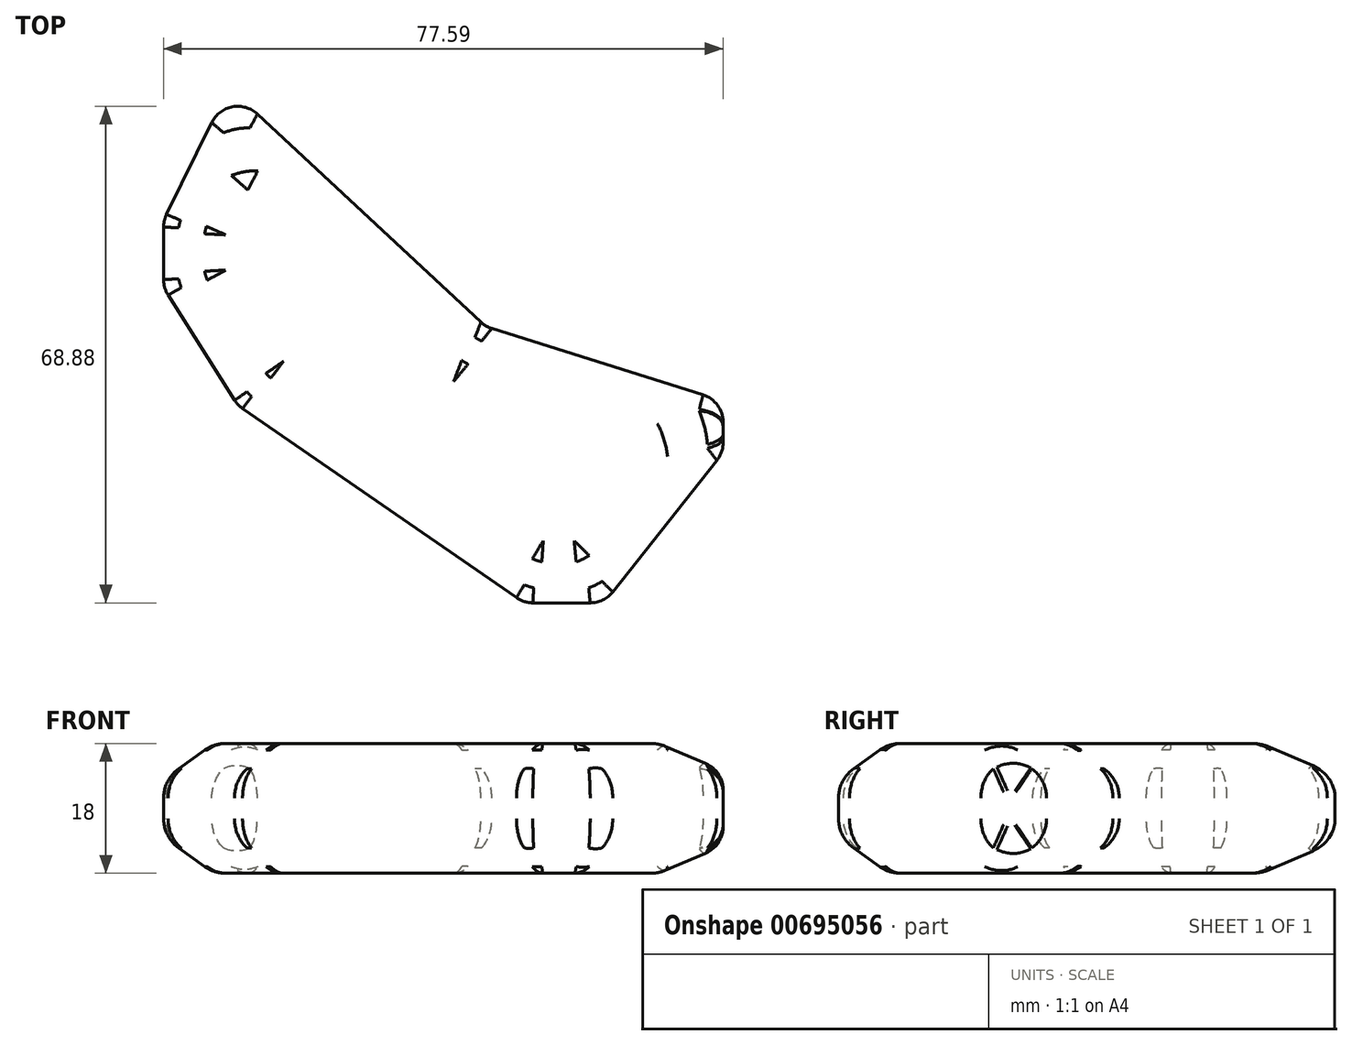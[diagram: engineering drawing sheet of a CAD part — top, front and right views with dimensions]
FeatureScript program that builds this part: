
annotation { "Feature Type Name" : "Feature", "Feature Type Description" : "" }
export const myFeature = defineFeature(function(context is Context, id is Id, definition is map)
    precondition{}
    {
        {
            var Q0;
            Q0=qCreatedBy(makeId("Top.planeOp"),FACE);
            var sketch = newSketch(context, id + "F0", { "sketchPlane" : qUnion([Q0])});
            skCircle(sketch, "E0", {"center": v(11.86, 12.18) * mm, "radius": 17 * mm, "construction": true});
            skLineSegment(sketch, "E1", {"start": v(0, 0) * mm, "end": v(35.6, -33.14) * mm});
            skLineSegment(sketch, "E2", {"start": v(35.6, -33.14) * mm, "end": v(68.53, -43.5) * mm});
            skLineSegment(sketch, "E3", {"start": v(68.53, -43.5) * mm, "end": v(68.53, -50.63) * mm});
            skLineSegment(sketch, "E4", {"start": v(68.53, -50.63) * mm, "end": v(52.03, -71.47) * mm});
            skLineSegment(sketch, "E5", {"start": v(52.03, -71.47) * mm, "end": v(40.9, -71.47) * mm});
            skLineSegment(sketch, "E6", {"start": v(40.9, -71.47) * mm, "end": v(1.22, -44.06) * mm});
            skLineSegment(sketch, "E7", {"start": v(1.22, -44.06) * mm, "end": v(-9.06, -27.79) * mm});
            skLineSegment(sketch, "E8", {"start": v(-9.06, -27.79) * mm, "end": v(-9.06, -18.41) * mm});
            skLineSegment(sketch, "E9", {"start": v(-9.06, -18.41) * mm, "end": v(0, 0) * mm});
            skSolve(sketch);
        }
        {
            var Q0;
            Q0=makeQuery(id+"F0.imprint","IMPRINT",FACE,{"disambiguationData":[TD([[makeQuery(id+"F0.imprint","IMPRINT",EDGE,{"derivedFrom":sQuery(id+"F0.wireOp",EDGE,"E1")}),-1.0]])]});
            extrude(context, id + "F1", {"entities" : qUnion([Q0]), "depth" : 9 * mm, "offsetDistance" : 25 * mm, "hasSecondDirection" : true, "secondDirectionOppositeDirection" : true, "secondDirectionDepth" : 9 * mm});
        }
        {
            var Q0;
            Q0=makeQuery(id+"F1.opExtrude","CAP_FACE",FACE,{"disambiguationData":[OSD([sQuery(id+"F0.wireOp",EDGE,"E1"),sQuery(id+"F0.wireOp",EDGE,"E2"),sQuery(id+"F0.wireOp",EDGE,"E3"),sQuery(id+"F0.wireOp",EDGE,"E4"),sQuery(id+"F0.wireOp",EDGE,"E5"),sQuery(id+"F0.wireOp",EDGE,"E6"),sQuery(id+"F0.wireOp",EDGE,"E7"),sQuery(id+"F0.wireOp",EDGE,"E8"),sQuery(id+"F0.wireOp",EDGE,"E9")])],"isStart":false});
            chamfer(context, id + "F2", {"entities" : qUnion([Q0]), "chamferType" : ChamferType.TWO_OFFSETS, "width1" : 5 * mm, "oppositeDirection" : false, "width2" : 7 * mm, "tangentPropagation" : true});
        }
        {
            var Q0;
            Q0=makeQuery(id+"F1.opExtrude","CAP_FACE",FACE,{"disambiguationData":[OSD([sQuery(id+"F0.wireOp",EDGE,"E1"),sQuery(id+"F0.wireOp",EDGE,"E2"),sQuery(id+"F0.wireOp",EDGE,"E3"),sQuery(id+"F0.wireOp",EDGE,"E4"),sQuery(id+"F0.wireOp",EDGE,"E5"),sQuery(id+"F0.wireOp",EDGE,"E6"),sQuery(id+"F0.wireOp",EDGE,"E7"),sQuery(id+"F0.wireOp",EDGE,"E8"),sQuery(id+"F0.wireOp",EDGE,"E9")])],"isStart":true});
            chamfer(context, id + "F3", {"entities" : qUnion([Q0]), "chamferType" : ChamferType.TWO_OFFSETS, "width1" : 7 * mm, "oppositeDirection" : false, "width2" : 5 * mm, "tangentPropagation" : true});
        }
        {
            var Q0;
            Q0=makeQuery(id+"F1.opExtrude","CAP_FACE",FACE,{"disambiguationData":[OSD([sQuery(id+"F0.wireOp",EDGE,"E1"),sQuery(id+"F0.wireOp",EDGE,"E2"),sQuery(id+"F0.wireOp",EDGE,"E3"),sQuery(id+"F0.wireOp",EDGE,"E4"),sQuery(id+"F0.wireOp",EDGE,"E5"),sQuery(id+"F0.wireOp",EDGE,"E6"),sQuery(id+"F0.wireOp",EDGE,"E7"),sQuery(id+"F0.wireOp",EDGE,"E8"),sQuery(id+"F0.wireOp",EDGE,"E9")])],"isStart":true});
            var Q1;
            Q1=makeQuery(id+"F1.opExtrude","CAP_FACE",FACE,{"disambiguationData":[OSD([sQuery(id+"F0.wireOp",EDGE,"E1"),sQuery(id+"F0.wireOp",EDGE,"E2"),sQuery(id+"F0.wireOp",EDGE,"E3"),sQuery(id+"F0.wireOp",EDGE,"E4"),sQuery(id+"F0.wireOp",EDGE,"E5"),sQuery(id+"F0.wireOp",EDGE,"E6"),sQuery(id+"F0.wireOp",EDGE,"E7"),sQuery(id+"F0.wireOp",EDGE,"E8"),sQuery(id+"F0.wireOp",EDGE,"E9")])],"isStart":false});
            var Q2;
            {var subQ0=sQuery(id+"F0.wireOp",EDGE,"E2");Q2=makeQuery(id+"F3.opChamfer","BLEND_EDGE",EDGE,{"blendedFrom":[makeQuery(id+"F1.opExtrude","CAP_EDGE",EDGE,{"disambiguationData":[OSD([subQ0])],"isStart":true}),makeQuery(id+"F1.opExtrude","SWEPT_FACE",FACE,{"disambiguationData":[OSD([subQ0])]})],"blendedInto":[makeQuery(id+"F1.opExtrude","SWEPT_FACE",FACE,{"disambiguationData":[OSD([subQ0])]})]});}
            var Q3;
            {var subQ0=sQuery(id+"F0.wireOp",EDGE,"E2");Q3=makeQuery(id+"F2.opChamfer","BLEND_EDGE",EDGE,{"blendedFrom":[makeQuery(id+"F1.opExtrude","CAP_EDGE",EDGE,{"disambiguationData":[OSD([subQ0])],"isStart":false}),makeQuery(id+"F1.opExtrude","SWEPT_FACE",FACE,{"disambiguationData":[OSD([subQ0])]})],"blendedInto":[makeQuery(id+"F1.opExtrude","SWEPT_FACE",FACE,{"disambiguationData":[OSD([subQ0])]})]});}
            var Q4;
            {var subQ0=sQuery(id+"F0.wireOp",EDGE,"E1");Q4=makeQuery(id+"F2.opChamfer","BLEND_EDGE",EDGE,{"blendedFrom":[makeQuery(id+"F1.opExtrude","CAP_EDGE",EDGE,{"disambiguationData":[OSD([subQ0])],"isStart":false}),makeQuery(id+"F1.opExtrude","SWEPT_FACE",FACE,{"disambiguationData":[OSD([subQ0])]})],"blendedInto":[makeQuery(id+"F1.opExtrude","SWEPT_FACE",FACE,{"disambiguationData":[OSD([subQ0])]})]});}
            var Q5;
            {var subQ0=sQuery(id+"F0.wireOp",EDGE,"E1");Q5=makeQuery(id+"F3.opChamfer","BLEND_EDGE",EDGE,{"blendedFrom":[makeQuery(id+"F1.opExtrude","CAP_EDGE",EDGE,{"disambiguationData":[OSD([subQ0])],"isStart":true}),makeQuery(id+"F1.opExtrude","SWEPT_FACE",FACE,{"disambiguationData":[OSD([subQ0])]})],"blendedInto":[makeQuery(id+"F1.opExtrude","SWEPT_FACE",FACE,{"disambiguationData":[OSD([subQ0])]})]});}
            var Q6;
            {var subQ0=sQuery(id+"F0.wireOp",EDGE,"E9");Q6=makeQuery(id+"F3.opChamfer","BLEND_EDGE",EDGE,{"blendedFrom":[makeQuery(id+"F1.opExtrude","CAP_EDGE",EDGE,{"disambiguationData":[OSD([subQ0])],"isStart":true}),makeQuery(id+"F1.opExtrude","SWEPT_FACE",FACE,{"disambiguationData":[OSD([subQ0])]})],"blendedInto":[makeQuery(id+"F1.opExtrude","SWEPT_FACE",FACE,{"disambiguationData":[OSD([subQ0])]})]});}
            var Q7;
            {var subQ0=sQuery(id+"F0.wireOp",EDGE,"E9");Q7=makeQuery(id+"F2.opChamfer","BLEND_EDGE",EDGE,{"blendedFrom":[makeQuery(id+"F1.opExtrude","CAP_EDGE",EDGE,{"disambiguationData":[OSD([subQ0])],"isStart":false}),makeQuery(id+"F1.opExtrude","SWEPT_FACE",FACE,{"disambiguationData":[OSD([subQ0])]})],"blendedInto":[makeQuery(id+"F1.opExtrude","SWEPT_FACE",FACE,{"disambiguationData":[OSD([subQ0])]})]});}
            var Q8;
            {var subQ0=sQuery(id+"F0.wireOp",EDGE,"E4");Q8=makeQuery(id+"F3.opChamfer","BLEND_EDGE",EDGE,{"blendedFrom":[makeQuery(id+"F1.opExtrude","CAP_EDGE",EDGE,{"disambiguationData":[OSD([subQ0])],"isStart":true}),makeQuery(id+"F1.opExtrude","SWEPT_FACE",FACE,{"disambiguationData":[OSD([subQ0])]})],"blendedInto":[makeQuery(id+"F1.opExtrude","SWEPT_FACE",FACE,{"disambiguationData":[OSD([subQ0])]})]});}
            var Q9;
            {var subQ0=sQuery(id+"F0.wireOp",EDGE,"E4");Q9=makeQuery(id+"F2.opChamfer","BLEND_EDGE",EDGE,{"blendedFrom":[makeQuery(id+"F1.opExtrude","CAP_EDGE",EDGE,{"disambiguationData":[OSD([subQ0])],"isStart":false}),makeQuery(id+"F1.opExtrude","SWEPT_FACE",FACE,{"disambiguationData":[OSD([subQ0])]})],"blendedInto":[makeQuery(id+"F1.opExtrude","SWEPT_FACE",FACE,{"disambiguationData":[OSD([subQ0])]})]});}
            var Q10;
            {var subQ0=sQuery(id+"F0.wireOp",EDGE,"E5");Q10=makeQuery(id+"F3.opChamfer","BLEND_EDGE",EDGE,{"blendedFrom":[makeQuery(id+"F1.opExtrude","CAP_EDGE",EDGE,{"disambiguationData":[OSD([subQ0])],"isStart":true}),makeQuery(id+"F1.opExtrude","SWEPT_FACE",FACE,{"disambiguationData":[OSD([subQ0])]})],"blendedInto":[makeQuery(id+"F1.opExtrude","SWEPT_FACE",FACE,{"disambiguationData":[OSD([subQ0])]})]});}
            var Q11;
            {var subQ0=sQuery(id+"F0.wireOp",EDGE,"E5");Q11=makeQuery(id+"F2.opChamfer","BLEND_EDGE",EDGE,{"blendedFrom":[makeQuery(id+"F1.opExtrude","CAP_EDGE",EDGE,{"disambiguationData":[OSD([subQ0])],"isStart":false}),makeQuery(id+"F1.opExtrude","SWEPT_FACE",FACE,{"disambiguationData":[OSD([subQ0])]})],"blendedInto":[makeQuery(id+"F1.opExtrude","SWEPT_FACE",FACE,{"disambiguationData":[OSD([subQ0])]})]});}
            var Q12;
            {var subQ0=sQuery(id+"F0.wireOp",EDGE,"E6");Q12=makeQuery(id+"F3.opChamfer","BLEND_EDGE",EDGE,{"blendedFrom":[makeQuery(id+"F1.opExtrude","CAP_EDGE",EDGE,{"disambiguationData":[OSD([subQ0])],"isStart":true}),makeQuery(id+"F1.opExtrude","SWEPT_FACE",FACE,{"disambiguationData":[OSD([subQ0])]})],"blendedInto":[makeQuery(id+"F1.opExtrude","SWEPT_FACE",FACE,{"disambiguationData":[OSD([subQ0])]})]});}
            var Q13;
            {var subQ0=sQuery(id+"F0.wireOp",EDGE,"E6");Q13=makeQuery(id+"F2.opChamfer","BLEND_EDGE",EDGE,{"blendedFrom":[makeQuery(id+"F1.opExtrude","CAP_EDGE",EDGE,{"disambiguationData":[OSD([subQ0])],"isStart":false}),makeQuery(id+"F1.opExtrude","SWEPT_FACE",FACE,{"disambiguationData":[OSD([subQ0])]})],"blendedInto":[makeQuery(id+"F1.opExtrude","SWEPT_FACE",FACE,{"disambiguationData":[OSD([subQ0])]})]});}
            var Q14;
            {var subQ0=sQuery(id+"F0.wireOp",EDGE,"E7");Q14=makeQuery(id+"F2.opChamfer","BLEND_EDGE",EDGE,{"blendedFrom":[makeQuery(id+"F1.opExtrude","CAP_EDGE",EDGE,{"disambiguationData":[OSD([subQ0])],"isStart":false}),makeQuery(id+"F1.opExtrude","SWEPT_FACE",FACE,{"disambiguationData":[OSD([subQ0])]})],"blendedInto":[makeQuery(id+"F1.opExtrude","SWEPT_FACE",FACE,{"disambiguationData":[OSD([subQ0])]})]});}
            var Q15;
            {var subQ0=sQuery(id+"F0.wireOp",EDGE,"E8");Q15=makeQuery(id+"F2.opChamfer","BLEND_EDGE",EDGE,{"blendedFrom":[makeQuery(id+"F1.opExtrude","CAP_EDGE",EDGE,{"disambiguationData":[OSD([subQ0])],"isStart":false}),makeQuery(id+"F1.opExtrude","SWEPT_FACE",FACE,{"disambiguationData":[OSD([subQ0])]})],"blendedInto":[makeQuery(id+"F1.opExtrude","SWEPT_FACE",FACE,{"disambiguationData":[OSD([subQ0])]})]});}
            var Q16;
            {var subQ0=sQuery(id+"F0.wireOp",EDGE,"E8");Q16=makeQuery(id+"F3.opChamfer","BLEND_EDGE",EDGE,{"blendedFrom":[makeQuery(id+"F1.opExtrude","CAP_EDGE",EDGE,{"disambiguationData":[OSD([subQ0])],"isStart":true}),makeQuery(id+"F1.opExtrude","SWEPT_FACE",FACE,{"disambiguationData":[OSD([subQ0])]})],"blendedInto":[makeQuery(id+"F1.opExtrude","SWEPT_FACE",FACE,{"disambiguationData":[OSD([subQ0])]})]});}
            var Q17;
            {var subQ0=sQuery(id+"F0.wireOp",EDGE,"E7");Q17=makeQuery(id+"F3.opChamfer","BLEND_EDGE",EDGE,{"blendedFrom":[makeQuery(id+"F1.opExtrude","CAP_EDGE",EDGE,{"disambiguationData":[OSD([subQ0])],"isStart":true}),makeQuery(id+"F1.opExtrude","SWEPT_FACE",FACE,{"disambiguationData":[OSD([subQ0])]})],"blendedInto":[makeQuery(id+"F1.opExtrude","SWEPT_FACE",FACE,{"disambiguationData":[OSD([subQ0])]})]});}
            fillet(context, id + "F4", {"entities" : qUnion([Q0, Q1, Q2, Q3, Q4, Q5, Q6, Q7, Q8, Q9, Q10, Q11, Q12, Q13, Q14, Q15, Q16, Q17]), "radius" : 5 * mm, "tangentPropagation" : true, "allowEdgeOverflow" : false});
        }
        {
            var Q0;
            Q0=makeQuery(id+"F1.opExtrude","SWEPT_FACE",FACE,{"disambiguationData":[OSD([sQuery(id+"F0.wireOp",EDGE,"E3")])]});
            var Q1;
            Q1=makeQuery(id+"F1.opExtrude","SWEPT_EDGE",EDGE,{"disambiguationData":[OSD([sQuery(id+"F0.wireOp",EDGE,"E4"),sQuery(id+"F0.wireOp",EDGE,"E5")])]});
            var Q2;
            Q2=makeQuery(id+"F1.opExtrude","SWEPT_EDGE",EDGE,{"disambiguationData":[OSD([sQuery(id+"F0.wireOp",EDGE,"E5"),sQuery(id+"F0.wireOp",EDGE,"E6")])]});
            var Q3;
            Q3=makeQuery(id+"F1.opExtrude","SWEPT_EDGE",EDGE,{"disambiguationData":[OSD([sQuery(id+"F0.wireOp",EDGE,"E6"),sQuery(id+"F0.wireOp",EDGE,"E7")])]});
            var Q4;
            Q4=makeQuery(id+"F1.opExtrude","SWEPT_EDGE",EDGE,{"disambiguationData":[OSD([sQuery(id+"F0.wireOp",EDGE,"E7"),sQuery(id+"F0.wireOp",EDGE,"E8")])]});
            var Q5;
            Q5=makeQuery(id+"F1.opExtrude","SWEPT_EDGE",EDGE,{"disambiguationData":[OSD([sQuery(id+"F0.wireOp",EDGE,"E8"),sQuery(id+"F0.wireOp",EDGE,"E9")])]});
            var Q6;
            Q6=makeQuery(id+"F1.opExtrude","SWEPT_EDGE",EDGE,{"disambiguationData":[OSD([sQuery(id+"F0.wireOp",EDGE,"E1"),sQuery(id+"F0.wireOp",EDGE,"E2")])]});
            var Q7;
            Q7=makeQuery(id+"F1.opExtrude","SWEPT_EDGE",EDGE,{"disambiguationData":[OSD([sQuery(id+"F0.wireOp",EDGE,"E1"),sQuery(id+"F0.wireOp",EDGE,"E9")])]});
            fillet(context, id + "F5", {"entities" : qUnion([Q0, Q1, Q2, Q3, Q4, Q5, Q6, Q7]), "radius" : 4 * mm, "tangentPropagation" : true, "allowEdgeOverflow" : false});
        }
        {
            var Q0;
            Q0=makeQuery(id+"F2.opChamfer","BLEND_EDGE",EDGE,{"blendedFrom":[makeQuery(id+"F1.opExtrude","CAP_EDGE",EDGE,{"disambiguationData":[OSD([sQuery(id+"F0.wireOp",EDGE,"E2")])],"isStart":false}),makeQuery(id+"F1.opExtrude","CAP_EDGE",EDGE,{"disambiguationData":[OSD([sQuery(id+"F0.wireOp",EDGE,"E4")])],"isStart":false})],"blendedInto":[]});
            var Q1;
            Q1=makeQuery(id+"F3.opChamfer","BLEND_EDGE",EDGE,{"blendedFrom":[makeQuery(id+"F1.opExtrude","CAP_EDGE",EDGE,{"disambiguationData":[OSD([sQuery(id+"F0.wireOp",EDGE,"E2")])],"isStart":true}),makeQuery(id+"F1.opExtrude","CAP_EDGE",EDGE,{"disambiguationData":[OSD([sQuery(id+"F0.wireOp",EDGE,"E4")])],"isStart":true})],"blendedInto":[]});
            fillet(context, id + "F6", {"entities" : qUnion([Q0, Q1]), "radius" : 5 * mm, "tangentPropagation" : true, "allowEdgeOverflow" : false});
        }
    });
